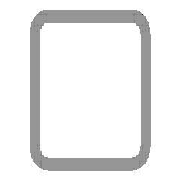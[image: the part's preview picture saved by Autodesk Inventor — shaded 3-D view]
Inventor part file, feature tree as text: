
AUTODESK INVENTOR PART (.ipt)
format: ipt  version: 2025.3 (Build 293356030, 356C)  size: 155,136 bytes
history: native  units: mm (DEFAULTED — no unit token found)
features: other x4, plane x3, split x2, sketch x1
ambient origin geometry x8: Origin, YZ Plane, XZ Plane, XY Plane, X Axis, Y Axis, Z Axis, Center Point
bodies: Solid1 (feature_tree), Body (feature_tree)
feature tree (10):
  parser-record x1  (decoder bookkeeping rows leaked as tree rows — omitted from the tree; the rows remain in map.json)
  other  "Driven Length"
  other  "Start Plane"
  other  "End Plane"
  plane  "Work Plane4"
  split  "Split1"
  plane  "Work Plane5"
  split  "Split2"
  sketch  "Sketch3"  dims[d3=2216.344931mm d4=0.0mm d7=6.0mm d9=80.0mm d11=80.0mm d12=3.0mm d13=-14.545455mm d14=2201.799476mm d15=40.0mm d16=40.0mm d17=90.0deg d18=2216.344931mm]
  plane  "Work Plane3"
